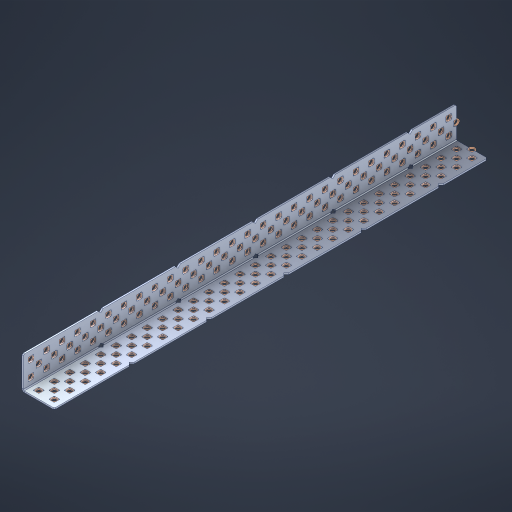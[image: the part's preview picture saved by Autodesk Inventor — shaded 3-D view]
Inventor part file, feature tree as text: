
AUTODESK INVENTOR PART (.ipt)
format: ipt  version: 2023 (Build 270158000, 158)  size: 1,964,544 bytes
history: native  units: in
note: dims shown in document units (in); Inventor stores cm internally (conversion verified against a paired STEP export)
features: other x174, extrude x166, sheet_metal_op x8, sketch x7, pattern_linear x2, mirror x1, chamfer x1
ambient origin geometry x8: Origin, YZ Plane, XZ Plane, XY Plane, X Axis, Y Axis, Z Axis, Center Point
bodies: Solid1 (feature_tree), Body (feature_tree)
feature tree (359):
  sheet_metal_op  "Flanges"
  sheet_metal_op  "Body Pattern"
  pattern_linear  "Center Pattern"  Spacing1=1.0in  [1 undecoded]
  other  "Arc Length"
  pattern_linear  "Notch Pattern"  Spacing1=0.1875in  [1 undecoded]
  other  "Diagonal Plane"
  mirror  "Everything Mirrored"
  chamfer  "End Chamfer"
  sketch  "Sketch1"  dims[d0=1.0in]
  other  "Plate1"
  sketch  "Sketch2"  dims[d1=14.0in]
  other  "Plate2"
  sheet_metal_op  "Bend1"
  sheet_metal_op  "Corner1"
  sketch  "Sketch8"  dims[d2=0.0469in]
  sketch  "Sketch9"  dims[d3=0.0469in]
  other  "Srf91"
  sheet_metal_op  "Body Pattern Sketch"
  other  "Srf92"
  sketch  "Sketch13"  dims[d4=0.0234in]
  sketch  "Sketch15"  dims[d5=0.0938in]
  sketch  "Sketch16"  dims[d6=0.0469in d7=1.0in d8=90.0deg d9=0.0312in d10=0.1875in d11=0.0469in d12=0.0469in d49=0.182in d50=0.02in d52=0.25in d53=0.0469in d54=0.0in d55=0.172in d56=1.0in d57=0.0in d60=11.0236in d62=0.5in d63=0.7874in d65=0.5in d85=0.1473in d86=0.1659in d89=0.0469in d90=0.0in d91=0.04in d92=0.0491in d95=2.5in d96=0.04in d97=0.25in d98=45.0deg d99=0.25in d106=0.182in d107=0.02in d108=0.5in d110=0.0469in d111=0.0in d112=0.172in d113=0.5in d114=0.0in d117=0.5in d123=0.25in d125=0.25in d126=0.0491in d127=0.1227in d128=0.08in d129=0.04in d130=2.5in]
  other  "Srf786"
  other  "Srf856"
  other  "Srf857"
  other  "Srf858"
  other  "Srf859"
  other  "Srf860"
  other  "Srf861"
  other  "Srf889"
  other  "Srf890"
  other  "Srf891"
  other  "Srf1275"
  other  "Srf1276"
  other  "Srf1278"
  other  "Srf1279"
  other  "Srf1280"
  other  "Srf1281"
  other  "Srf1282"
  other  "Srf1283"
  other  "Srf1277"
  other  "Srf1285"
  other  "Srf1286"
  other  "Srf1287"
  other  "Srf1383"
  other  "Srf1384"
  other  "Srf1385"
  other  "Srf1386"
  other  "Srf1387"
  other  "Srf1388"
  other  "Srf1389"
  other  "Srf1390"
  other  "Srf1391"
  other  "Srf1392"
  other  "Srf1393"
  other  "Srf1394"
  other  "Srf1395"
  other  "Srf1396"
  other  "Srf1397"
  other  "Srf1398"
  other  "Srf1399"
  other  "Srf1400"
  other  "Srf1401"
  other  "Srf1402"
  other  "Srf1403"
  other  "Srf1404"
  other  "Srf1405"
  other  "Srf1406"
  other  "Srf1407"
  other  "Srf1408"
  other  "Srf1409"
  other  "Srf1410"
  other  "Srf1411"
  other  "Srf1412"
  other  "Srf1413"
  other  "Srf1414"
  other  "Srf1415"
  other  "Srf1416"
  other  "Srf1417"
  other  "Srf1418"
  other  "Srf1419"
  other  "Srf1420"
  other  "Srf1421"
  other  "Srf1422"
  other  "Srf1423"
  other  "Srf1424"
  other  "Srf1425"
  other  "Srf1426"
  other  "Srf1427"
  other  "Srf1428"
  other  "Srf1429"
  other  "Srf1430"
  other  "Srf1445"
  other  "Srf1446"
  other  "Srf1447"
  other  "Srf1448"
  other  "Srf1449"
  other  "Srf1450"
  other  "Srf1451"
  other  "Srf1452"
  other  "Srf1453"
  other  "Srf1454"
  other  "Srf1455"
  other  "Srf1456"
  other  "Srf1457"
  other  "Srf1458"
  other  "Srf1459"
  other  "Srf1460"
  other  "Srf1461"
  other  "Srf1462"
  other  "Srf1463"
  other  "Srf1464"
  other  "Srf1465"
  other  "Srf1466"
  other  "Srf1467"
  other  "Srf1468"
  other  "Srf1475"
  other  "Srf1476"
  other  "Srf1477"
  other  "Srf1478"
  other  "Srf1479"
  other  "Srf1480"
  other  "Srf1481"
  other  "Srf1482"
  other  "Srf1483"
  other  "Srf1484"
  other  "Srf1485"
  other  "Srf1486"
  other  "Srf1487"
  other  "Srf1488"
  other  "Srf1489"
  other  "Srf1490"
  other  "Srf1491"
  other  "Srf1492"
  other  "Srf1493"
  other  "Srf1494"
  other  "Srf1495"
  other  "Srf1496"
  other  "Srf1497"
  other  "Srf1498"
  other  "Srf1499"
  other  "Srf1500"
  other  "Srf1501"
  other  "Srf1502"
  other  "Srf1503"
  other  "Srf1504"
  other  "Srf1505"
  other  "Srf1506"
  other  "Srf1507"
  other  "Srf1508"
  other  "Srf1509"
  other  "Srf1510"
  other  "Srf1511"
  other  "Srf1512"
  other  "Srf1513"
  other  "Srf1514"
  other  "Srf1515"
  other  "Srf1516"
  other  "Srf1517"
  other  "Srf1518"
  other  "Srf1519"
  other  "Srf1520"
  other  "Srf1521"
  other  "Srf1522"
  other  "Srf1537"
  other  "Srf1538"
  other  "Srf1539"
  other  "Srf1540"
  other  "Srf1541"
  other  "Srf1542"
  other  "Srf1543"
  other  "Srf1544"
  other  "Srf1545"
  other  "Srf1546"
  other  "Srf1547"
  other  "Srf1548"
  other  "Srf1549"
  other  "Srf1550"
  other  "Srf1551"
  other  "Srf1552"
  other  "Srf1553"
  other  "Srf1554"
  other  "Srf1555"
  other  "Srf1556"
  other  "Srf1557"
  other  "Srf1558"
  other  "Srf1559"
  other  "Srf1560"
  sheet_metal_op  "Body Stamp"
  sheet_metal_op  "Body Circle"
  other  "Center Stamp"
  other  "Center Circle"
  sheet_metal_op  "Notch"
  extrude  "ExtrusionSrf92"  Depth=0.0469in
  extrude  "ExtrusionSrf856"  Depth=0.0469in
  extrude  "ExtrusionSrf857"  Depth=0.182in
  extrude  "ExtrusionSrf858"  Depth=0.02in
  extrude  "ExtrusionSrf859"  Depth=0.25in
  extrude  "ExtrusionSrf860"  Depth=0.0469in
  extrude  "ExtrusionSrf861"  TaperAngle=0.0deg  [1 undecoded]
  extrude  "ExtrusionSrf889"  Depth=2.5in
  extrude  "ExtrusionSrf890"  Depth=1.0in TaperAngle=0.0deg
  extrude  "ExtrusionSrf891"  Depth=2.5in
  extrude  "ExtrusionSrf1275"  Depth=0.5in
  extrude  "ExtrusionSrf1276"  Depth=2.5in
  extrude  "ExtrusionSrf1277"  Depth=2.5in
  extrude  "ExtrusionSrf1278"  Depth=0.0469in
  extrude  "ExtrusionSrf1279"  Depth=2.5in TaperAngle=0.0deg
  extrude  "ExtrusionSrf1280"  Depth=2.5in
  extrude  "ExtrusionSrf1281"  Depth=0.25in TaperAngle=45.0deg
  extrude  "ExtrusionSrf1282"  Depth=0.25in
  extrude  "ExtrusionSrf1345"  Depth=0.182in
  extrude  "ExtrusionSrf1346"  Depth=0.02in
  extrude  "ExtrusionSrf1347"  Depth=0.5in
  extrude  "ExtrusionSrf1348"  Depth=0.0469in
  extrude  "ExtrusionSrf1383"  TaperAngle=0.0deg  [1 undecoded]
  extrude  "ExtrusionSrf1384"  Depth=2.5in
  extrude  "ExtrusionSrf1385"  Depth=0.5in TaperAngle=0.0deg
  extrude  "ExtrusionSrf1386"  Depth=0.5in
  extrude  "ExtrusionSrf1387"  Depth=0.25in
  extrude  "ExtrusionSrf1388"  Depth=0.25in
  extrude  "ExtrusionSrf1389"  Depth=2.5in
  extrude  "ExtrusionSrf1390"  Depth=2.5in
  extrude  "ExtrusionSrf1391"  Depth=2.5in
  extrude  "ExtrusionSrf1392"  Depth=2.5in
  extrude  "ExtrusionSrf1393"  Depth=2.5in
  extrude  "ExtrusionSrf1394"  [1 undecoded]
  extrude  "ExtrusionSrf1395"  [1 undecoded]
  extrude  "ExtrusionSrf1396"  [1 undecoded]
  extrude  "ExtrusionSrf1397"  [1 undecoded]
  extrude  "ExtrusionSrf1398"  [1 undecoded]
  extrude  "ExtrusionSrf1399"  [1 undecoded]
  extrude  "ExtrusionSrf1400"  [1 undecoded]
  extrude  "ExtrusionSrf1401"  [1 undecoded]
  extrude  "ExtrusionSrf1402"  [1 undecoded]
  extrude  "ExtrusionSrf1403"  [1 undecoded]
  extrude  "ExtrusionSrf1404"  [1 undecoded]
  extrude  "ExtrusionSrf1405"  [1 undecoded]
  extrude  "ExtrusionSrf1406"  [1 undecoded]
  extrude  "ExtrusionSrf1407"  [1 undecoded]
  extrude  "ExtrusionSrf1408"  [1 undecoded]
  extrude  "ExtrusionSrf1409"  [1 undecoded]
  extrude  "ExtrusionSrf1410"  [1 undecoded]
  extrude  "ExtrusionSrf1411"  [1 undecoded]
  extrude  "ExtrusionSrf1412"  [1 undecoded]
  extrude  "ExtrusionSrf1413"  [1 undecoded]
  extrude  "ExtrusionSrf1414"  [1 undecoded]
  extrude  "ExtrusionSrf1415"  [1 undecoded]
  extrude  "ExtrusionSrf1416"  [1 undecoded]
  extrude  "ExtrusionSrf1417"  [1 undecoded]
  extrude  "ExtrusionSrf1418"  [1 undecoded]
  extrude  "ExtrusionSrf1419"  [1 undecoded]
  extrude  "ExtrusionSrf1420"  [1 undecoded]
  extrude  "ExtrusionSrf1421"  [1 undecoded]
  extrude  "ExtrusionSrf1422"  [1 undecoded]
  extrude  "ExtrusionSrf1423"  [1 undecoded]
  extrude  "ExtrusionSrf1424"  [1 undecoded]
  extrude  "ExtrusionSrf1425"  [1 undecoded]
  extrude  "ExtrusionSrf1426"  [1 undecoded]
  extrude  "ExtrusionSrf1427"  [1 undecoded]
  extrude  "ExtrusionSrf1428"  [1 undecoded]
  extrude  "ExtrusionSrf1429"  [1 undecoded]
  extrude  "ExtrusionSrf1430"  [1 undecoded]
  extrude  "ExtrusionSrf1445"  [1 undecoded]
  extrude  "ExtrusionSrf1446"  [1 undecoded]
  extrude  "ExtrusionSrf1447"  [1 undecoded]
  extrude  "ExtrusionSrf1448"  [1 undecoded]
  extrude  "ExtrusionSrf1449"  [1 undecoded]
  extrude  "ExtrusionSrf1450"  [1 undecoded]
  extrude  "ExtrusionSrf1451"  [1 undecoded]
  extrude  "ExtrusionSrf1452"  [1 undecoded]
  extrude  "ExtrusionSrf1453"  [1 undecoded]
  extrude  "ExtrusionSrf1454"  [1 undecoded]
  extrude  "ExtrusionSrf1455"  [1 undecoded]
  extrude  "ExtrusionSrf1456"  [1 undecoded]
  extrude  "ExtrusionSrf1457"  [1 undecoded]
  extrude  "ExtrusionSrf1458"  [1 undecoded]
  extrude  "ExtrusionSrf1459"  [1 undecoded]
  extrude  "ExtrusionSrf1460"  [1 undecoded]
  extrude  "ExtrusionSrf1461"  [1 undecoded]
  extrude  "ExtrusionSrf1462"  [1 undecoded]
  extrude  "ExtrusionSrf1463"  [1 undecoded]
  extrude  "ExtrusionSrf1464"  [1 undecoded]
  extrude  "ExtrusionSrf1465"  [1 undecoded]
  extrude  "ExtrusionSrf1466"  [1 undecoded]
  extrude  "ExtrusionSrf1467"  [1 undecoded]
  extrude  "ExtrusionSrf1468"  [1 undecoded]
  extrude  "ExtrusionSrf1475"  [1 undecoded]
  extrude  "ExtrusionSrf1476"  [1 undecoded]
  extrude  "ExtrusionSrf1477"  [1 undecoded]
  extrude  "ExtrusionSrf1478"  [1 undecoded]
  extrude  "ExtrusionSrf1479"  [1 undecoded]
  extrude  "ExtrusionSrf1480"  [1 undecoded]
  extrude  "ExtrusionSrf1481"  [1 undecoded]
  extrude  "ExtrusionSrf1482"  [1 undecoded]
  extrude  "ExtrusionSrf1483"  [1 undecoded]
  extrude  "ExtrusionSrf1484"  [1 undecoded]
  extrude  "ExtrusionSrf1485"  [1 undecoded]
  extrude  "ExtrusionSrf1486"  [1 undecoded]
  extrude  "ExtrusionSrf1487"  [1 undecoded]
  extrude  "ExtrusionSrf1488"  [1 undecoded]
  extrude  "ExtrusionSrf1489"  [1 undecoded]
  extrude  "ExtrusionSrf1490"  [1 undecoded]
  extrude  "ExtrusionSrf1491"  [1 undecoded]
  extrude  "ExtrusionSrf1492"  [1 undecoded]
  extrude  "ExtrusionSrf1493"  [1 undecoded]
  extrude  "ExtrusionSrf1494"  [1 undecoded]
  extrude  "ExtrusionSrf1495"  [1 undecoded]
  extrude  "ExtrusionSrf1496"  [1 undecoded]
  extrude  "ExtrusionSrf1497"  [1 undecoded]
  extrude  "ExtrusionSrf1498"  [1 undecoded]
  extrude  "ExtrusionSrf1499"  [1 undecoded]
  extrude  "ExtrusionSrf1500"  [1 undecoded]
  extrude  "ExtrusionSrf1501"  [1 undecoded]
  extrude  "ExtrusionSrf1502"  [1 undecoded]
  extrude  "ExtrusionSrf1503"  [1 undecoded]
  extrude  "ExtrusionSrf1504"  [1 undecoded]
  extrude  "ExtrusionSrf1505"  [1 undecoded]
  extrude  "ExtrusionSrf1506"  [1 undecoded]
  extrude  "ExtrusionSrf1507"  [1 undecoded]
  extrude  "ExtrusionSrf1508"  [1 undecoded]
  extrude  "ExtrusionSrf1509"  [1 undecoded]
  extrude  "ExtrusionSrf1510"  [1 undecoded]
  extrude  "ExtrusionSrf1511"  [1 undecoded]
  extrude  "ExtrusionSrf1512"  [1 undecoded]
  extrude  "ExtrusionSrf1513"  [1 undecoded]
  extrude  "ExtrusionSrf1514"  [1 undecoded]
  extrude  "ExtrusionSrf1515"  [1 undecoded]
  extrude  "ExtrusionSrf1516"  [1 undecoded]
  extrude  "ExtrusionSrf1517"  [1 undecoded]
  extrude  "ExtrusionSrf1518"  [1 undecoded]
  extrude  "ExtrusionSrf1519"  [1 undecoded]
  extrude  "ExtrusionSrf1520"  [1 undecoded]
  extrude  "ExtrusionSrf1521"  [1 undecoded]
  extrude  "ExtrusionSrf1522"  [1 undecoded]
  extrude  "ExtrusionSrf1537"  [1 undecoded]
  extrude  "ExtrusionSrf1538"  [1 undecoded]
  extrude  "ExtrusionSrf1539"  [1 undecoded]
  extrude  "ExtrusionSrf1540"  [1 undecoded]
  extrude  "ExtrusionSrf1541"  [1 undecoded]
  extrude  "ExtrusionSrf1542"  [1 undecoded]
  extrude  "ExtrusionSrf1543"  [1 undecoded]
  extrude  "ExtrusionSrf1544"  [1 undecoded]
  extrude  "ExtrusionSrf1545"  [1 undecoded]
  extrude  "ExtrusionSrf1546"  [1 undecoded]
  extrude  "ExtrusionSrf1547"  [1 undecoded]
  extrude  "ExtrusionSrf1548"  [1 undecoded]
  extrude  "ExtrusionSrf1549"  [1 undecoded]
  extrude  "ExtrusionSrf1550"  [1 undecoded]
  extrude  "ExtrusionSrf1551"  [1 undecoded]
  extrude  "ExtrusionSrf1552"  [1 undecoded]
  extrude  "ExtrusionSrf1553"  [1 undecoded]
  extrude  "ExtrusionSrf1554"  [1 undecoded]
  extrude  "ExtrusionSrf1555"  [1 undecoded]
  extrude  "ExtrusionSrf1556"  [1 undecoded]
  extrude  "ExtrusionSrf1557"  [1 undecoded]
  extrude  "ExtrusionSrf1558"  [1 undecoded]
  extrude  "ExtrusionSrf1559"  [1 undecoded]
  extrude  "ExtrusionSrf1560"  [1 undecoded]
note: 137 required parameter values undecoded (feature->parameter linkage not recoverable at this tier; creation-order binding heuristic only, values carry confidence <= 0.55)
